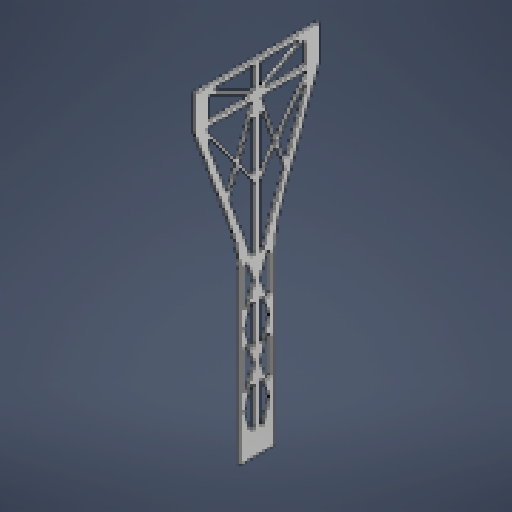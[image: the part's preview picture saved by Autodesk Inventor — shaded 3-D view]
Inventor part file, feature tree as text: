
AUTODESK INVENTOR PART (.ipt)
format: ipt  version: 2024.3 (Build 283343000, 343)  size: 439,296 bytes
history: native  units: mm (DEFAULTED — no unit token found)
features: other x5, sketch x2, sheet_metal_op x1, mirror x1, chamfer x1, projected_geometry x1
ambient origin geometry x8: Origin, YZ Plane, XZ Plane, XY Plane, X Axis, Y Axis, Z Axis, Center Point
bodies: Solid2_1 (feature_tree)
feature tree (11):
  other  "PLATE,ARM,TOP.ipt"
  sheet_metal_op  "Face1"
  mirror  "Mirror1"
  chamfer  "Corner Round1"
  sketch  "Sketch2"  dims[d6=177.8mm]
  other  "Plate1"
  sketch  "Sketch3"  dims[d7=596.9mm d8=152.4mm d9=12.217305mm d10=50.8mm d11=25.4mm d12=127.0mm d13=3.175mm d14=19.05mm d15=6.35mm d16=3.175mm d17=38.1mm d18=6.35mm d19=9.525mm d20=6.35mm d21=1.5875mm d23=3.175mm d24=6.35mm d25=6.35mm d26=3.175mm d27=96.515487mm d28=20.0mm d30=102.865487mm d31=10.0mm d33=25.4mm d35=3.175mm d36=0.0mm d37=3.175mm d38=10.0mm d39=3.175mm]
  projected_geometry  "Projected Loop1"
  other  "Solid2::PLATE,ARM,TOP.ipt"
  other  "TaggingFeature1"
  other  "Cut1"
